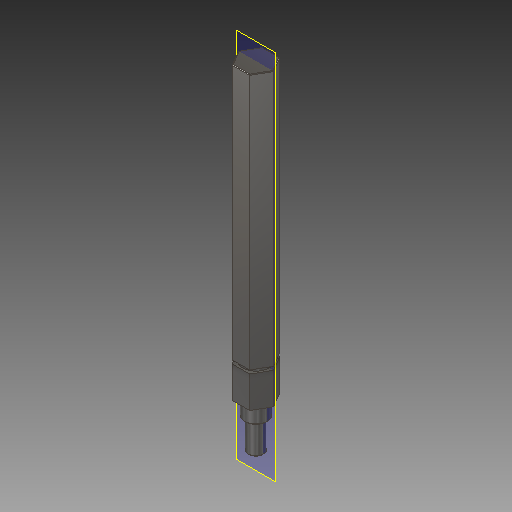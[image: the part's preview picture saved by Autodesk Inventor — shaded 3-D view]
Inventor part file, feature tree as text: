
AUTODESK INVENTOR PART (.ipt)
format: ipt  version: 2018 (Build 220112000, 112)  size: 129,024 bytes
history: native  units: in
note: dims shown in document units (in); Inventor stores cm internally (conversion verified against a paired STEP export)
features: plane x1, chamfer x1
ambient origin geometry x8: Origin, YZ Plane, XZ Plane, XY Plane, X Axis, Y Axis, Z Axis, Center Point
bodies: Solid1 (feature_tree)
feature tree (2):
  plane  "Work Plane1"
  chamfer  "Chamfer1"  [1 undecoded]
note: 1 required parameter value undecoded (feature->parameter linkage not recoverable at this tier; creation-order binding heuristic only, values carry confidence <= 0.55)
